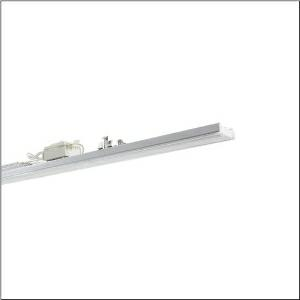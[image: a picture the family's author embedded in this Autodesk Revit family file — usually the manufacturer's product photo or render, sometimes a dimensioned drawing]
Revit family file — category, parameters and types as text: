
# Revit family: licross_21_recessed_mo_52tl11dn4axg
name_source: partatom
category: Lighting Fixtures
units: mm (PartAtom-declared; Revit-internal decimal feet)

## family parameters
Cut with Voids When Loaded = No
Host = Face
Light Source = No
Part Type = Normal
Room Calculation Point = No
Round Connector Dimension = Use Diameter
Shared = No

## types (1)
- --- (1 x LED, 10120 lm, 58 W, 4000K)
    Apparent Load = 58 VA
    CIE Flux Codes = 89 96 99 100 100
    Color Rendering = 80
    Color Temperature = 4000K
    Default Elevation = 1800 mm
    Description = Licross 21 Recessed MO, luminaire insert, of sheet steel, galvanised, coil coated, white, length: 1.500mm, width: 66mm, height: 67mm, LED rated luminous flux: 10.120lm, light colour: 840, SDCM (Standard Deviation of Colour Matching)MacAdam ≤ 3 SDCM (initial), control gear: DALI 2, with plug, 5-pole, with phase selection, mains connection: 220..240V, AC, 50/60Hz, rated input power: 58W, internal wiring halogen-free, primary light control with lens, of plastic, primary optical cover: cover, of PMMA, light emission: direct distribution, primary light characteristic: symmetric, protection rating (complete): IP40, insulation class (complete): insulation class I (protective earthing), certification: CE, ENEC, VDE, UKCA, protection symbol: D if used in an environment without relevant dust loads with corresponding accessories, impact resistance: IK06, permissible ambient temperature for indoor applications: -25..+40°C, corresponds to IFS (International Featured Standards) requirements for safety and quality in the food industry, reducing of maximum allowable ambient temperature of 5°C with ceiling mounting, LABS conformity tested according to VDMA 24364:2018-05, The light source and the operating device comply with the requirements of the Ecodesign Regulation (EU) 2019/2020 and are replaceable in accordance with this regulation, packaging unit: 1 piece
    Height = 58 mm
    Lamp = 1 x LED
    Lamp Light Flux = 10120 lm
    Lamp Power = 58 W
    Lamp count = 1
    Length = 1500 mm
    Luminous efficacy = 174 lm/W
    Manufacturer = Siteco
    ModVariant = No
    Model = 52TL11DN4AXG
    Mounting Place = Ceiling
    Mounting Type = Pendant
    Number of Poles = 1
    OnlyDefault = Yes
    Power Factor = 1
    Product Name = Licross 21 Recessed MO
    Product group = luminaire insert | ceiling pendant
    ProductGroupID = 901
    Protection Class = Protection class I
    Protection Degree = IP 40
    RLX_Detail_Level = 1
    RLX_Emergency_Light_Flux = 0 lm
    RLX_Emergency_Type = 0
    RLX_Emergency_Type_DB = No
    RlxData = <blob elided: 24753 chars, md5=3ffe8733>
    Socket = socket
    Standby Power = 0 W
    System Light Flux = 10120 lm
    System Power = 58 W
    Type Comments = factory setting: luminous flux: 100 % | dim-lin: 254 | 390 mA
    Type Image = l_1296930.jpg
    URL = http://relux.com
    VarID = @adj_127133
    Voltage = 0 V
    Weight = 0.00 kg
    Width = 66 mm

## geometry (parser evidence)
native form markers: Blend x4, Sweep x12
no freeform markers — native parametric forms only
